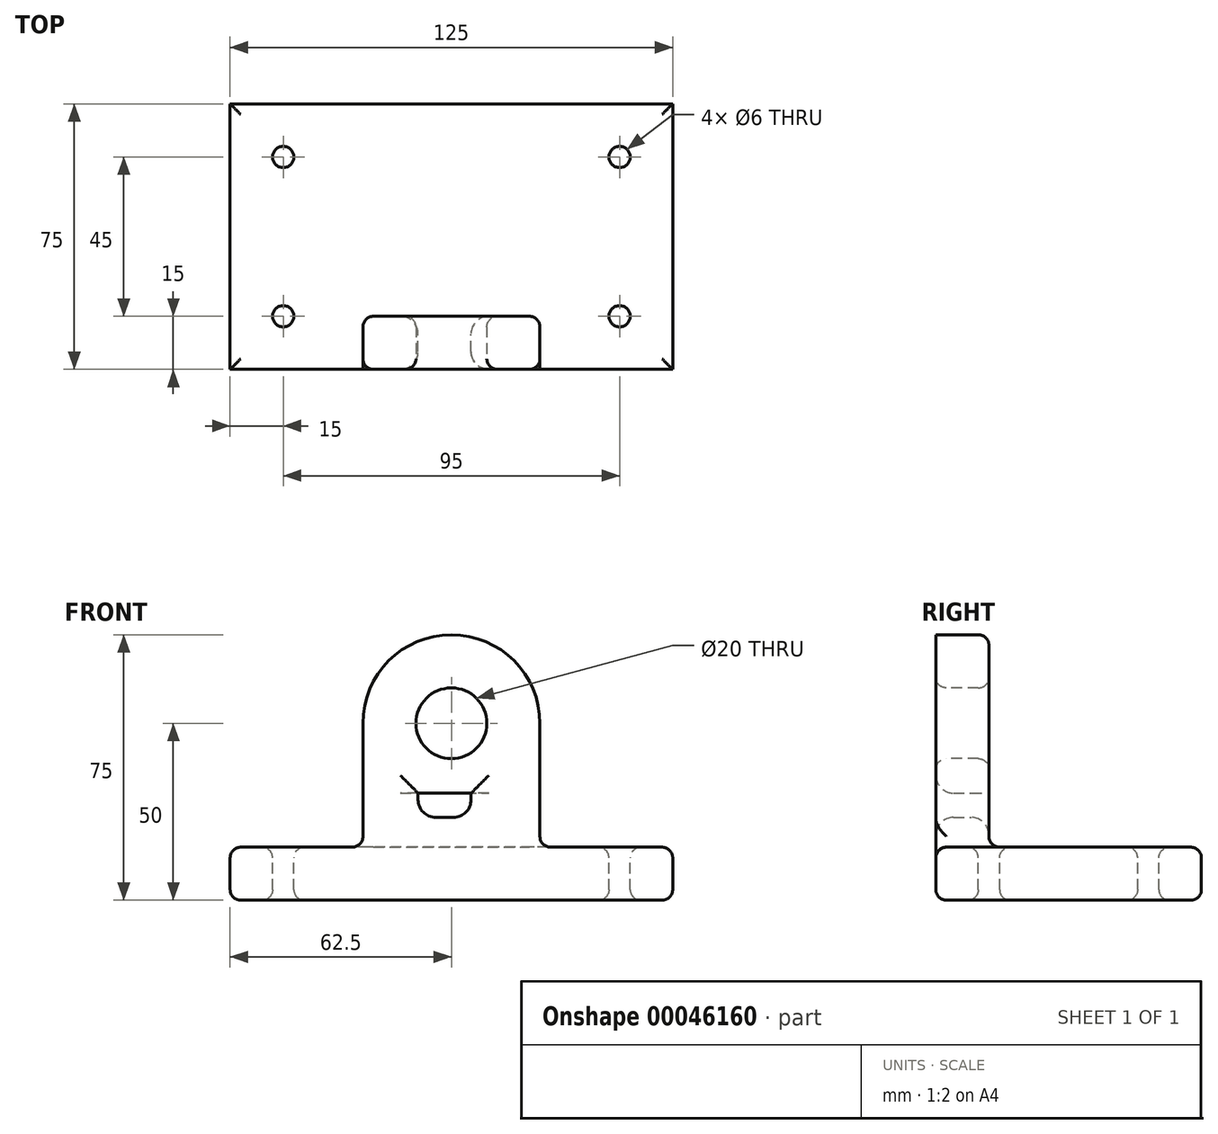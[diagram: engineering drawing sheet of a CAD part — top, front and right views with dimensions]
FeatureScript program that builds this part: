
annotation { "Feature Type Name" : "Feature", "Feature Type Description" : "" }
export const myFeature = defineFeature(function(context is Context, id is Id, definition is map)
    precondition{}
    {
        {
            var Q0;
            Q0=qCreatedBy(makeId("Top.planeOp"),FACE);
            var sketch = newSketch(context, id + "F0", { "sketchPlane" : qUnion([Q0])});
            skLineSegment(sketch, "E0.rect.bottom", {"start": v(62.5, 37.5) * mm, "end": v(-62.5, 37.5) * mm});
            skLineSegment(sketch, "E0.rect.top", {"start": v(62.5, -37.5) * mm, "end": v(-62.5, -37.5) * mm});
            skLineSegment(sketch, "E0.rect.left", {"start": v(62.5, 37.5) * mm, "end": v(62.5, -37.5) * mm});
            skLineSegment(sketch, "E0.rect.right", {"start": v(-62.5, 37.5) * mm, "end": v(-62.5, -37.5) * mm});
            skPoint(sketch, "E0.rect.middle", {"position": v(0, 0) * mm});
            skSolve(sketch);
        }
        {
            var Q0;
            Q0=makeQuery(id+"F0.imprint","IMPRINT",FACE,{"disambiguationData":[TD([[makeQuery(id+"F0.imprint","IMPRINT",EDGE,{"derivedFrom":sQuery(id+"F0.wireOp",EDGE,"E0.rect.bottom")}),1.0]])]});
            extrude(context, id + "F1", {"entities" : qUnion([Q0]), "depth" : 15 * mm});
        }
        {
            var Q0;
            Q0=makeQuery(id+"F1.opExtrude","SWEPT_FACE",FACE,{"disambiguationData":[OSD([sQuery(id+"F0.wireOp",EDGE,"E0.rect.top")])]});
            var sketch = newSketch(context, id + "F2", { "sketchPlane" : qUnion([Q0])});
            skLineSegment(sketch, "E1", {"start": v(0, 0) * mm, "end": v(0, 50) * mm, "construction": true});
            skPoint(sketch, "E1.endSnap0", {"position": v(0, 15) * mm});
            skCircle(sketch, "E2", {"center": v(0, 50) * mm, "radius": 25 * mm});
            skLineSegment(sketch, "E3.bottom", {"start": v(-25, 50) * mm, "end": v(25, 50) * mm});
            skLineSegment(sketch, "E3.top", {"start": v(-25, 0) * mm, "end": v(25, 0) * mm});
            skLineSegment(sketch, "E3.left", {"start": v(-25, 50) * mm, "end": v(-25, 0) * mm});
            skLineSegment(sketch, "E3.right", {"start": v(25, 50) * mm, "end": v(25, 0) * mm});
            skCircle(sketch, "E4", {"center": v(0, 50) * mm, "radius": 10 * mm});
            skSolve(sketch);
        }
        {
            var Q0;
            {var subQ0=sQuery(id+"F2.wireOp",EDGE,"E3.bottom");Q0=makeQuery(id+"F2.imprint","IMPRINT",FACE,{"disambiguationData":[TD([[makeQuery(id+"F2.imprint","IMPRINT",EDGE,{"derivedFrom":subQ0}),1.0]])]});}
            var Q1;
            {var subQ0=sQuery(id+"F2.wireOp",EDGE,"E3.bottom");Q1=makeQuery(id+"F2.imprint","IMPRINT",FACE,{"disambiguationData":[TD([[makeQuery(id+"F2.imprint","IMPRINT",EDGE,{"derivedFrom":subQ0}),-1.0]])]});}
            var Q2;
            {var subQ0=makeQuery(id+"F1.opExtrude","CAP_EDGE",EDGE,{"disambiguationData":[OSD([sQuery(id+"F0.wireOp",EDGE,"E0.rect.top")])],"isStart":false});var subQ3=sQuery(id+"F2.wireOp",EDGE,"E3.left");var subQ4=makeQuery(id+"F2.imprint","INTERSECT",VERTEX,{"derivedFrom":[subQ0,subQ3]});Q2=makeQuery(id+"F2.imprint","IMPRINT",FACE,{"disambiguationData":[TD([[makeQuery(id+"F2.imprint","IMPRINT",EDGE,{"disambiguationData":[TD([[subQ4,1.0]])],"derivedFrom":subQ0}),-1.0]])]});}
            var Q3;
            {var subQ5=sQuery(id+"F2.wireOp",EDGE,"E3.top");Q3=makeQuery(id+"F2.imprint","IMPRINT",FACE,{"disambiguationData":[TD([[makeQuery(id+"F2.imprint","IMPRINT",EDGE,{"derivedFrom":subQ5}),-1.0]])]});}
            var Q4;
            Q4=makeQuery(id+"F1.opExtrude","SWEPT_FACE",FACE,{"disambiguationData":[OSD([sQuery(id+"F0.wireOp",EDGE,"E0.rect.bottom")])]});
            extrude(context, id + "F3", {"entities" : qUnion([Q0, Q1, Q2, Q3]), "operationType" : NewBodyOperationType.ADD, "oppositeDirection" : true, "endBoundEntityFace" : qUnion([Q4]), "depth" : 15 * mm});
        }
        {
            var Q0;
            Q0=makeQuery(id+"F1.opExtrude","CAP_FACE",FACE,{"disambiguationData":[OSD([sQuery(id+"F0.wireOp",EDGE,"E0.rect.bottom"),sQuery(id+"F0.wireOp",EDGE,"E0.rect.top"),sQuery(id+"F0.wireOp",EDGE,"E0.rect.left"),sQuery(id+"F0.wireOp",EDGE,"E0.rect.right")])],"isStart":false});
            var sketch = newSketch(context, id + "F4", { "sketchPlane" : qUnion([Q0])});
            skLineSegment(sketch, "E5.rect.bottom", {"start": v(47.5, -22.5) * mm, "end": v(-47.5, -22.5) * mm, "construction": true});
            skLineSegment(sketch, "E5.rect.top", {"start": v(47.5, 22.5) * mm, "end": v(-47.5, 22.5) * mm, "construction": true});
            skLineSegment(sketch, "E5.rect.left", {"start": v(47.5, -22.5) * mm, "end": v(47.5, 22.5) * mm, "construction": true});
            skLineSegment(sketch, "E5.rect.right", {"start": v(-47.5, -22.5) * mm, "end": v(-47.5, 22.5) * mm, "construction": true});
            skPoint(sketch, "E5.rect.middle", {"position": v(0, 0) * mm});
            skCircle(sketch, "E6", {"center": v(-47.5, 22.5) * mm, "radius": 3 * mm});
            skCircle(sketch, "E7", {"center": v(-47.5, -22.5) * mm, "radius": 3 * mm});
            skCircle(sketch, "E8", {"center": v(47.5, 22.5) * mm, "radius": 3 * mm});
            skCircle(sketch, "E9", {"center": v(47.5, -22.5) * mm, "radius": 3 * mm});
            skSolve(sketch);
        }
        {
            var Q0;
            Q0=makeQuery(id+"F4.imprint","IMPRINT",FACE,{"disambiguationData":[TD([[makeQuery(id+"F4.imprint","IMPRINT",EDGE,{"derivedFrom":sQuery(id+"F4.wireOp",EDGE,"E7")}),1.0]])]});
            var Q1;
            Q1=makeQuery(id+"F4.imprint","IMPRINT",FACE,{"disambiguationData":[TD([[makeQuery(id+"F4.imprint","IMPRINT",EDGE,{"derivedFrom":sQuery(id+"F4.wireOp",EDGE,"E8")}),1.0]])]});
            var Q2;
            Q2=makeQuery(id+"F4.imprint","IMPRINT",FACE,{"disambiguationData":[TD([[makeQuery(id+"F4.imprint","IMPRINT",EDGE,{"derivedFrom":sQuery(id+"F4.wireOp",EDGE,"E9")}),1.0]])]});
            var Q3;
            Q3=makeQuery(id+"F4.imprint","IMPRINT",FACE,{"disambiguationData":[TD([[makeQuery(id+"F4.imprint","IMPRINT",EDGE,{"derivedFrom":sQuery(id+"F4.wireOp",EDGE,"E6")}),1.0]])]});
            extrude(context, id + "F5", {"entities" : qUnion([Q0, Q1, Q2, Q3]), "operationType" : NewBodyOperationType.REMOVE, "endBound" : BoundingType.UP_TO_NEXT, "oppositeDirection" : true, "depth" : 25 * mm});
        }
        {
            var Q0;
            Q0=makeQuery(id+"F3.boolean.opBoolean","INTERSECT",EDGE,{"derivedFrom":[makeQuery(id+"F1.opExtrude","CAP_FACE",FACE,{"disambiguationData":[OSD([sQuery(id+"F0.wireOp",EDGE,"E0.rect.bottom"),sQuery(id+"F0.wireOp",EDGE,"E0.rect.top"),sQuery(id+"F0.wireOp",EDGE,"E0.rect.left"),sQuery(id+"F0.wireOp",EDGE,"E0.rect.right")])],"isStart":false}),makeQuery(id+"F3.opExtrude","SWEPT_FACE",FACE,{"disambiguationData":[OSD([sQuery(id+"F2.wireOp",EDGE,"E3.right")])]})]});
            var Q1;
            Q1=makeQuery(id+"F1.opExtrude","CAP_FACE",FACE,{"disambiguationData":[OSD([sQuery(id+"F0.wireOp",EDGE,"E0.rect.bottom"),sQuery(id+"F0.wireOp",EDGE,"E0.rect.top"),sQuery(id+"F0.wireOp",EDGE,"E0.rect.left"),sQuery(id+"F0.wireOp",EDGE,"E0.rect.right")])],"isStart":false});
            var Q2;
            Q2=makeQuery(id+"F1.opExtrude","CAP_FACE",FACE,{"disambiguationData":[OSD([sQuery(id+"F0.wireOp",EDGE,"E0.rect.bottom"),sQuery(id+"F0.wireOp",EDGE,"E0.rect.top"),sQuery(id+"F0.wireOp",EDGE,"E0.rect.left"),sQuery(id+"F0.wireOp",EDGE,"E0.rect.right")])],"isStart":true});
            var Q3;
            Q3=makeQuery(id+"F3.opExtrude","CAP_FACE",FACE,{"disambiguationData":[OSD([sQuery(id+"F2.wireOp",EDGE,"E2"),sQuery(id+"F2.wireOp",EDGE,"E3.top"),sQuery(id+"F2.wireOp",EDGE,"E3.left"),sQuery(id+"F2.wireOp",EDGE,"E3.right"),sQuery(id+"F2.wireOp",EDGE,"E4")])],"isStart":false});
            var Q4;
            Q4=makeQuery(id+"F3.opExtrude","CAP_EDGE",EDGE,{"disambiguationData":[OSD([sQuery(id+"F2.wireOp",EDGE,"E4")])],"isStart":true});
            fillet(context, id + "F6", {"entities" : qUnion([Q0, Q1, Q2, Q3, Q4]), "radius" : 3 * mm, "tangentPropagation" : true, "allowEdgeOverflow" : false});
        }
        {
            var Q0;
            Q0=makeQuery(id+"F3.opExtrude","CAP_FACE",FACE,{"disambiguationData":[OSD([sQuery(id+"F2.wireOp",EDGE,"E2"),sQuery(id+"F2.wireOp",EDGE,"E3.top"),sQuery(id+"F2.wireOp",EDGE,"E3.left"),sQuery(id+"F2.wireOp",EDGE,"E3.right"),sQuery(id+"F2.wireOp",EDGE,"E4")])],"isStart":false});
            var sketch = newSketch(context, id + "F7", { "sketchPlane" : qUnion([Q0])});
            skLineSegment(sketch, "E10.bottom", {"start": v(9.41, 30.26) * mm, "end": v(-5.56, 30.26) * mm});
            skLineSegment(sketch, "E10.top", {"start": v(9.41, 23.42) * mm, "end": v(-5.56, 23.42) * mm});
            skLineSegment(sketch, "E10.left", {"start": v(9.41, 30.26) * mm, "end": v(9.41, 23.42) * mm});
            skLineSegment(sketch, "E10.right", {"start": v(-5.56, 30.26) * mm, "end": v(-5.56, 23.42) * mm});
            skSolve(sketch);
        }
        {
            var Q0;
            Q0=makeQuery(id+"F7.imprint","IMPRINT",FACE,{"disambiguationData":[TD([[makeQuery(id+"F7.imprint","IMPRINT",EDGE,{"derivedFrom":sQuery(id+"F7.wireOp",EDGE,"E10.bottom")}),1.0]])]});
            extrude(context, id + "F8", {"entities" : qUnion([Q0]), "operationType" : NewBodyOperationType.REMOVE, "oppositeDirection" : true, "depth" : 25 * mm});
        }
        {
            var Q0;
            Q0=makeQuery(id+"F8.boolean.opBoolean","INTERSECT",EDGE,{"derivedFrom":[makeQuery(id+"F3.boolean.opBoolean","MERGE",FACE,{"derivedFrom":[makeQuery(id+"F1.opExtrude","SWEPT_FACE",FACE,{"disambiguationData":[OSD([sQuery(id+"F0.wireOp",EDGE,"E0.rect.top")])]}),makeQuery(id+"F3.opExtrude","CAP_FACE",FACE,{"disambiguationData":[OSD([sQuery(id+"F2.wireOp",EDGE,"E2"),sQuery(id+"F2.wireOp",EDGE,"E3.top"),sQuery(id+"F2.wireOp",EDGE,"E3.left"),sQuery(id+"F2.wireOp",EDGE,"E3.right"),sQuery(id+"F2.wireOp",EDGE,"E4")])],"isStart":true})]}),makeQuery(id+"F8.opExtrude","SWEPT_FACE",FACE,{"disambiguationData":[OSD([sQuery(id+"F7.wireOp",EDGE,"E10.bottom")])]})]});
            var Q1;
            Q1=makeQuery(id+"F8.boolean.opBoolean","INTERSECT",EDGE,{"derivedFrom":[makeQuery(id+"F3.boolean.opBoolean","MERGE",FACE,{"derivedFrom":[makeQuery(id+"F1.opExtrude","SWEPT_FACE",FACE,{"disambiguationData":[OSD([sQuery(id+"F0.wireOp",EDGE,"E0.rect.top")])]}),makeQuery(id+"F3.opExtrude","CAP_FACE",FACE,{"disambiguationData":[OSD([sQuery(id+"F2.wireOp",EDGE,"E2"),sQuery(id+"F2.wireOp",EDGE,"E3.top"),sQuery(id+"F2.wireOp",EDGE,"E3.left"),sQuery(id+"F2.wireOp",EDGE,"E3.right"),sQuery(id+"F2.wireOp",EDGE,"E4")])],"isStart":true})]}),makeQuery(id+"F8.opExtrude","SWEPT_FACE",FACE,{"disambiguationData":[OSD([sQuery(id+"F7.wireOp",EDGE,"E10.right")])]})]});
            var Q2;
            Q2=makeQuery(id+"F8.boolean.opBoolean","INTERSECT",EDGE,{"derivedFrom":[makeQuery(id+"F3.boolean.opBoolean","MERGE",FACE,{"derivedFrom":[makeQuery(id+"F1.opExtrude","SWEPT_FACE",FACE,{"disambiguationData":[OSD([sQuery(id+"F0.wireOp",EDGE,"E0.rect.top")])]}),makeQuery(id+"F3.opExtrude","CAP_FACE",FACE,{"disambiguationData":[OSD([sQuery(id+"F2.wireOp",EDGE,"E2"),sQuery(id+"F2.wireOp",EDGE,"E3.top"),sQuery(id+"F2.wireOp",EDGE,"E3.left"),sQuery(id+"F2.wireOp",EDGE,"E3.right"),sQuery(id+"F2.wireOp",EDGE,"E4")])],"isStart":true})]}),makeQuery(id+"F8.opExtrude","SWEPT_FACE",FACE,{"disambiguationData":[OSD([sQuery(id+"F7.wireOp",EDGE,"E10.top")])]})]});
            var Q3;
            Q3=makeQuery(id+"F8.boolean.opBoolean","INTERSECT",EDGE,{"derivedFrom":[makeQuery(id+"F3.boolean.opBoolean","MERGE",FACE,{"derivedFrom":[makeQuery(id+"F1.opExtrude","SWEPT_FACE",FACE,{"disambiguationData":[OSD([sQuery(id+"F0.wireOp",EDGE,"E0.rect.top")])]}),makeQuery(id+"F3.opExtrude","CAP_FACE",FACE,{"disambiguationData":[OSD([sQuery(id+"F2.wireOp",EDGE,"E2"),sQuery(id+"F2.wireOp",EDGE,"E3.top"),sQuery(id+"F2.wireOp",EDGE,"E3.left"),sQuery(id+"F2.wireOp",EDGE,"E3.right"),sQuery(id+"F2.wireOp",EDGE,"E4")])],"isStart":true})]}),makeQuery(id+"F8.opExtrude","SWEPT_FACE",FACE,{"disambiguationData":[OSD([sQuery(id+"F7.wireOp",EDGE,"E10.left")])]})]});
            var Q4;
            Q4=makeQuery(id+"F8.boolean.opBoolean","COPY",EDGE,{"derivedFrom":makeQuery(id+"F8.opExtrude","SWEPT_EDGE",EDGE,{"disambiguationData":[OSD([sQuery(id+"F7.wireOp",EDGE,"E10.top"),sQuery(id+"F7.wireOp",EDGE,"E10.left")])]})});
            var Q5;
            Q5=makeQuery(id+"F8.boolean.opBoolean","COPY",EDGE,{"derivedFrom":makeQuery(id+"F8.opExtrude","SWEPT_EDGE",EDGE,{"disambiguationData":[OSD([sQuery(id+"F7.wireOp",EDGE,"E10.top"),sQuery(id+"F7.wireOp",EDGE,"E10.right")])]})});
            fillet(context, id + "F9", {"entities" : qUnion([Q0, Q1, Q2, Q3, Q4, Q5]), "radius" : 5 * mm, "tangentPropagation" : true, "allowEdgeOverflow" : false});
        }
        {
            var Q0;
            Q0=makeQuery(id+"F9.opFillet","BLEND_EDGE",EDGE,{"blendedFrom":[makeQuery(id+"F8.boolean.opBoolean","COPY",EDGE,{"derivedFrom":makeQuery(id+"F8.opExtrude","SWEPT_EDGE",EDGE,{"disambiguationData":[OSD([sQuery(id+"F7.wireOp",EDGE,"E10.top"),sQuery(id+"F7.wireOp",EDGE,"E10.right")])]})}),makeQuery(id+"F3.opExtrude","CAP_FACE",FACE,{"disambiguationData":[OSD([sQuery(id+"F2.wireOp",EDGE,"E2"),sQuery(id+"F2.wireOp",EDGE,"E3.top"),sQuery(id+"F2.wireOp",EDGE,"E3.left"),sQuery(id+"F2.wireOp",EDGE,"E3.right"),sQuery(id+"F2.wireOp",EDGE,"E4")])],"isStart":false})],"blendedInto":[makeQuery(id+"F3.opExtrude","CAP_FACE",FACE,{"disambiguationData":[OSD([sQuery(id+"F2.wireOp",EDGE,"E2"),sQuery(id+"F2.wireOp",EDGE,"E3.top"),sQuery(id+"F2.wireOp",EDGE,"E3.left"),sQuery(id+"F2.wireOp",EDGE,"E3.right"),sQuery(id+"F2.wireOp",EDGE,"E4")])],"isStart":false})]});
            var Q1;
            Q1=makeQuery(id+"F8.boolean.opBoolean","COPY",EDGE,{"derivedFrom":makeQuery(id+"F8.opExtrude","CAP_EDGE",EDGE,{"disambiguationData":[OSD([sQuery(id+"F7.wireOp",EDGE,"E10.bottom")])],"isStart":true})});
            fillet(context, id + "F10", {"entities" : qUnion([Q0, Q1]), "radius" : 5 * mm, "tangentPropagation" : true, "allowEdgeOverflow" : false});
        }
    });
